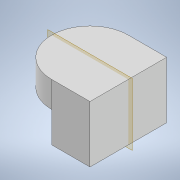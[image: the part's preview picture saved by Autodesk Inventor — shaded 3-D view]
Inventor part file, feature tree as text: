
AUTODESK INVENTOR PART (.ipt)
format: ipt  version: 2022.2 (Build 262287000, 287)  size: 111,616 bytes
history: native  units: mm
features: sketch x2, other x1, extrude x1, plane x1, revolve x1
ambient origin geometry x8: Origin, YZ Plane, XZ Plane, XY Plane, X Axis, Y Axis, Z Axis, Center Point
bodies: Solid1 (feature_tree)
feature tree (6):
  other  "Crank.ipt"
  extrude  "Extrusion1"  Depth=2.5mm
  plane  "Work Plane2"
  revolve  "Revolution1"  [1 undecoded]
  sketch  "Sketch1"  dims[d0=10.0mm d1=2.5mm]
  sketch  "Sketch3"  dims[d2=2.5mm d3=5.0mm d4=3.7mm d5=0.0mm d9=2.0mm d10=45.0deg d11=180.0deg d12=0.872665mm]
note: 1 required parameter value undecoded (feature->parameter linkage not recoverable at this tier; creation-order binding heuristic only, values carry confidence <= 0.55)
